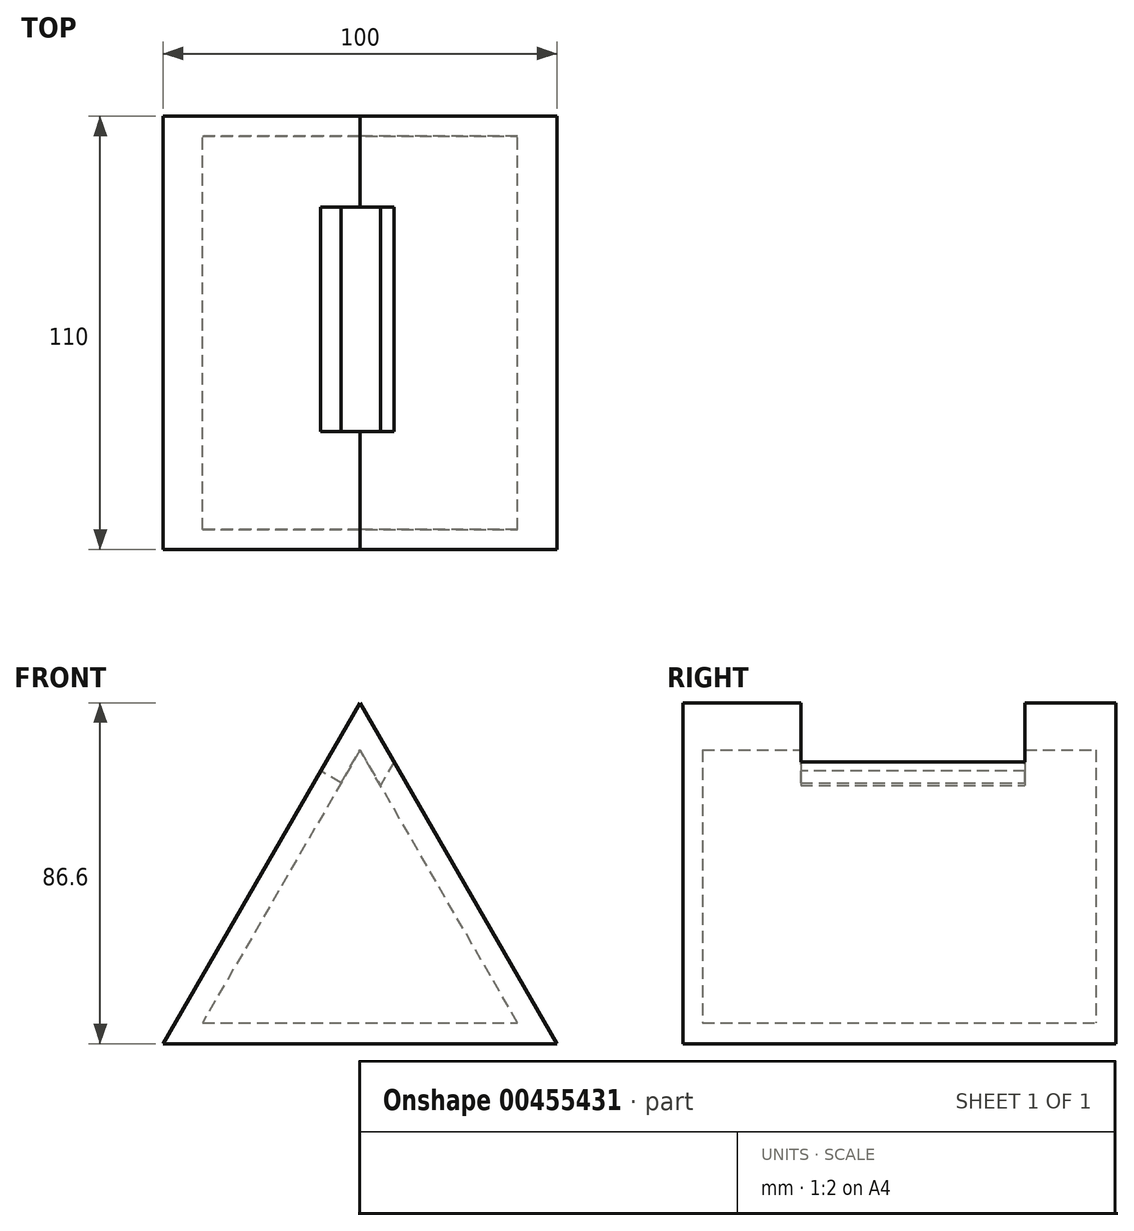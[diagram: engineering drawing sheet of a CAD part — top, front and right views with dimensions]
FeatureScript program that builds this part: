
annotation { "Feature Type Name" : "Feature", "Feature Type Description" : "" }
export const myFeature = defineFeature(function(context is Context, id is Id, definition is map)
    precondition{}
    {
        {
            var Q0;
            Q0=qCreatedBy(makeId("Front.planeOp"),FACE);
            var sketch = newSketch(context, id + "F0", { "sketchPlane" : qUnion([Q0])});
            skLineSegment(sketch, "E0", {"start": v(-50, 0) * mm, "end": v(0, 86.6) * mm});
            skLineSegment(sketch, "E1", {"start": v(0, 86.6) * mm, "end": v(50, 0) * mm});
            skLineSegment(sketch, "E2", {"start": v(50, 0) * mm, "end": v(-50, 0) * mm});
            skLineSegment(sketch, "E3", {"start": v(-40, 5.32) * mm, "end": v(40, 5.32) * mm});
            skLineSegment(sketch, "E4", {"start": v(40, 5.32) * mm, "end": v(0, 74.6) * mm});
            skLineSegment(sketch, "E5", {"start": v(0, 74.6) * mm, "end": v(-40, 5.32) * mm});
            skSolve(sketch);
        }
        {
            var Q0;
            Q0=makeQuery(id+"F0.imprint","IMPRINT",FACE,{"disambiguationData":[TD([[makeQuery(id+"F0.imprint","IMPRINT",EDGE,{"derivedFrom":sQuery(id+"F0.wireOp",EDGE,"E0")}),-1.0]])]});
            extrude(context, id + "F1", {"entities" : qUnion([Q0]), "depth" : 100 * mm});
        }
        {
            var Q0;
            Q0=makeQuery(id+"F1.opExtrude","CAP_FACE",FACE,{"disambiguationData":[OSD([sQuery(id+"F0.wireOp",EDGE,"E0"),sQuery(id+"F0.wireOp",EDGE,"E1"),sQuery(id+"F0.wireOp",EDGE,"E2"),sQuery(id+"F0.wireOp",EDGE,"E3"),sQuery(id+"F0.wireOp",EDGE,"E4"),sQuery(id+"F0.wireOp",EDGE,"E5")])],"isStart":false});
            var sketch = newSketch(context, id + "F2", { "sketchPlane" : qUnion([Q0])});
            skLineSegment(sketch, "E6", {"start": v(50, 0) * mm, "end": v(0, 86.6) * mm});
            skLineSegment(sketch, "E7", {"start": v(0, 86.6) * mm, "end": v(-50, 0) * mm});
            skLineSegment(sketch, "E8", {"start": v(-50, 0) * mm, "end": v(50, 0) * mm});
            skSolve(sketch);
        }
        {
            var Q0;
            Q0=makeQuery(id+"F2.imprint","IMPRINT",FACE,{"disambiguationData":[TD([[makeQuery(id+"F2.imprint","IMPRINT",EDGE,{"derivedFrom":sQuery(id+"F2.wireOp",EDGE,"E6")}),-1.0]])]});
            var Q1;
            Q1=makeQuery(id+"F2.imprint","IMPRINT",FACE,{"disambiguationData":[TD([[makeQuery(id+"F2.imprint","IMPRINT",EDGE,{"derivedFrom":makeQuery(id+"F1.opExtrude","CAP_EDGE",EDGE,{"disambiguationData":[OSD([sQuery(id+"F0.wireOp",EDGE,"E3")])],"isStart":false})}),1.0]])]});
            extrude(context, id + "F3", {"entities" : qUnion([Q0, Q1]), "operationType" : NewBodyOperationType.ADD, "depth" : 5 * mm});
        }
        {
            var Q0;
            Q0=makeQuery(id+"F1.opExtrude","CAP_FACE",FACE,{"disambiguationData":[OSD([sQuery(id+"F0.wireOp",EDGE,"E0"),sQuery(id+"F0.wireOp",EDGE,"E1"),sQuery(id+"F0.wireOp",EDGE,"E2"),sQuery(id+"F0.wireOp",EDGE,"E3"),sQuery(id+"F0.wireOp",EDGE,"E4"),sQuery(id+"F0.wireOp",EDGE,"E5")])],"isStart":true});
            var sketch = newSketch(context, id + "F4", { "sketchPlane" : qUnion([Q0])});
            skLineSegment(sketch, "E9", {"start": v(-50, 0) * mm, "end": v(0, 86.6) * mm});
            skLineSegment(sketch, "E10", {"start": v(0, 86.6) * mm, "end": v(50, 0) * mm});
            skLineSegment(sketch, "E11", {"start": v(50, 0) * mm, "end": v(-50, 0) * mm});
            skSolve(sketch);
        }
        {
            var Q0;
            Q0=makeQuery(id+"F4.imprint","IMPRINT",FACE,{"disambiguationData":[TD([[makeQuery(id+"F4.imprint","IMPRINT",EDGE,{"derivedFrom":makeQuery(id+"F1.opExtrude","CAP_EDGE",EDGE,{"disambiguationData":[OSD([sQuery(id+"F0.wireOp",EDGE,"E3")])],"isStart":true})}),-1.0]])]});
            var Q1;
            Q1=makeQuery(id+"F4.imprint","IMPRINT",FACE,{"disambiguationData":[TD([[makeQuery(id+"F4.imprint","IMPRINT",EDGE,{"derivedFrom":sQuery(id+"F4.wireOp",EDGE,"E9")}),1.0]])]});
            extrude(context, id + "F5", {"entities" : qUnion([Q0, Q1]), "operationType" : NewBodyOperationType.ADD, "depth" : 5 * mm});
        }
        {
            var Q0;
            Q0=makeQuery(id+"F5.boolean.opBoolean","MERGE",FACE,{"derivedFrom":[makeQuery(id+"F3.boolean.opBoolean","MERGE",FACE,{"derivedFrom":[makeQuery(id+"F1.opExtrude","SWEPT_FACE",FACE,{"disambiguationData":[OSD([sQuery(id+"F0.wireOp",EDGE,"E0")])]}),makeQuery(id+"F3.opExtrude","SWEPT_FACE",FACE,{"disambiguationData":[OSD([sQuery(id+"F2.wireOp",EDGE,"E7")])]})]}),makeQuery(id+"F5.opExtrude","SWEPT_FACE",FACE,{"disambiguationData":[OSD([sQuery(id+"F4.wireOp",EDGE,"E10")])]})]});
            var sketch = newSketch(context, id + "F6", { "sketchPlane" : qUnion([Q0])});
            skLineSegment(sketch, "E12.bottom", {"start": v(18.06, 75) * mm, "end": v(75.04, 75) * mm});
            skLineSegment(sketch, "E12.top", {"start": v(18.06, 55) * mm, "end": v(75.04, 55) * mm});
            skLineSegment(sketch, "E12.left", {"start": v(18.06, 75) * mm, "end": v(18.06, 55) * mm});
            skLineSegment(sketch, "E12.right", {"start": v(75.04, 75) * mm, "end": v(75.04, 55) * mm});
            skSolve(sketch);
        }
        {
            var Q0;
            Q0 = qSketchRegion(id + "F6", true);
            extrude(context, id + "F7", {"entities" : qUnion([Q0]), "operationType" : NewBodyOperationType.REMOVE, "oppositeDirection" : true, "depth" : 15 * mm});
        }
    });
